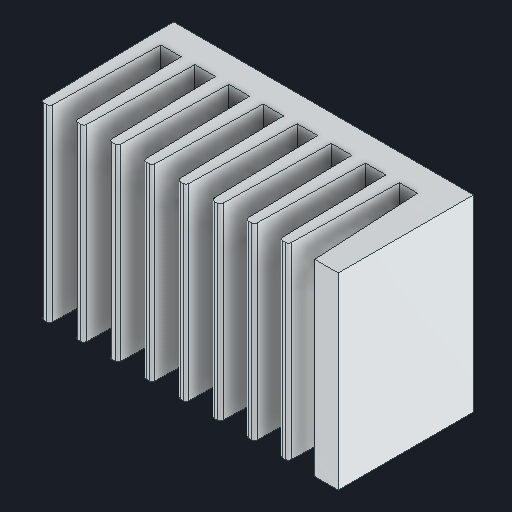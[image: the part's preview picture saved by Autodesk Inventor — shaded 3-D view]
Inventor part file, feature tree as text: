
AUTODESK INVENTOR PART (.ipt)
format: ipt  version: 2024 (Build 280153000, 153)  size: 169,472 bytes
history: native  units: mm
features: other x1, mirror x1
ambient origin geometry x8: Origin, YZ Plane, XZ Plane, XY Plane, X Axis, Y Axis, Z Axis, Center Point
bodies: Body1 (feature_tree)
feature tree (2):
  other  "Твердое тело1"
  mirror  "Mirror1"
